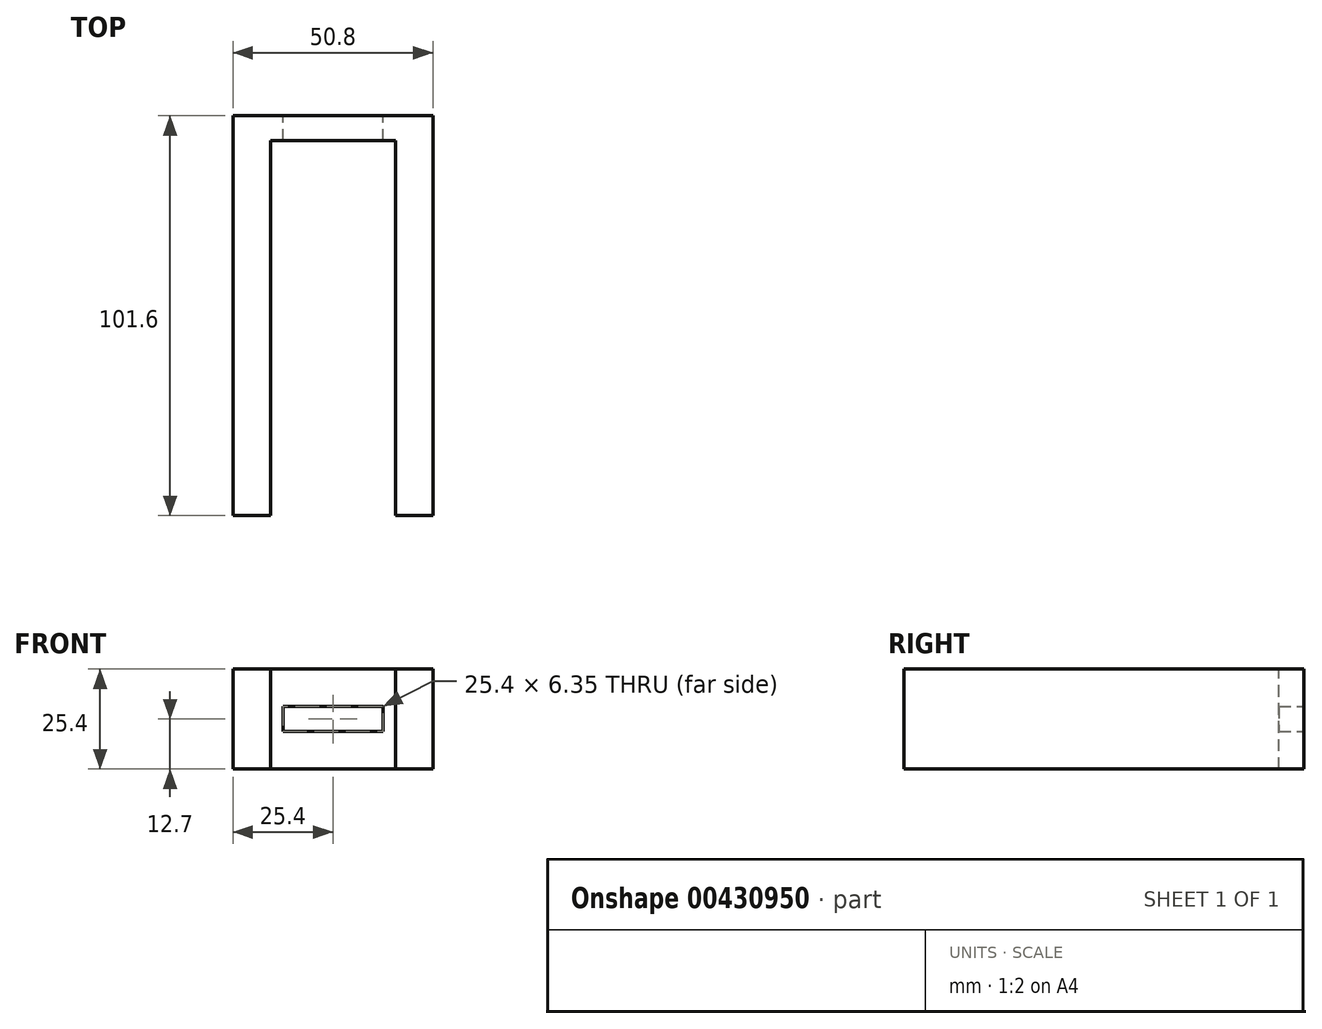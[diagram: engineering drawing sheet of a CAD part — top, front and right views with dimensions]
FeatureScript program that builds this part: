
annotation { "Feature Type Name" : "Feature", "Feature Type Description" : "" }
export const myFeature = defineFeature(function(context is Context, id is Id, definition is map)
    precondition{}
    {
        {
            var Q0;
            Q0=qCreatedBy(makeId("Front.planeOp"),FACE);
            var sketch = newSketch(context, id + "F0", { "sketchPlane" : qUnion([Q0])});
            skLineSegment(sketch, "E0.bottom", {"start": v(25.4, -12.7) * mm, "end": v(-25.4, -12.7) * mm});
            skLineSegment(sketch, "E0.top", {"start": v(25.4, 12.7) * mm, "end": v(-25.4, 12.7) * mm});
            skLineSegment(sketch, "E0.left", {"start": v(25.4, -12.7) * mm, "end": v(25.4, 12.7) * mm});
            skLineSegment(sketch, "E0.right", {"start": v(-25.4, -12.7) * mm, "end": v(-25.4, 12.7) * mm});
            skPoint(sketch, "E0.middle", {"position": v(0, 0) * mm});
            skLineSegment(sketch, "E1.bottom", {"start": v(12.7, 3.18) * mm, "end": v(-12.7, 3.18) * mm});
            skLineSegment(sketch, "E1.top", {"start": v(12.7, -3.17) * mm, "end": v(-12.7, -3.17) * mm});
            skLineSegment(sketch, "E1.left", {"start": v(12.7, 3.18) * mm, "end": v(12.7, -3.18) * mm});
            skLineSegment(sketch, "E1.right", {"start": v(-12.7, 3.18) * mm, "end": v(-12.7, -3.18) * mm});
            skLineSegment(sketch, "E2", {"start": v(-12.7, -3.17) * mm, "end": v(-12.7, -12.7) * mm});
            skLineSegment(sketch, "E3", {"start": v(-12.7, 3.18) * mm, "end": v(-12.7, 12.7) * mm});
            skLineSegment(sketch, "E4", {"start": v(12.7, -3.17) * mm, "end": v(12.7, -12.7) * mm});
            skLineSegment(sketch, "E5", {"start": v(12.7, 3.18) * mm, "end": v(12.7, 12.7) * mm});
            skLineSegment(sketch, "E6", {"start": v(15.88, 12.7) * mm, "end": v(15.88, -12.7) * mm});
            skLineSegment(sketch, "E7", {"start": v(-15.88, 12.7) * mm, "end": v(-15.88, -12.7) * mm});
            skSolve(sketch);
        }
        {
            var Q0;
            Q0 = qSketchRegion(id + "F0", true);
            extrude(context, id + "F1", {"entities" : qUnion([Q0]), "depth" : 6.35 * mm});
        }
        {
            var Q0;
            {var subQ0=sQuery(id+"F0.wireOp",EDGE,"E0.left");Q0=makeQuery(id+"F0.imprint","IMPRINT",FACE,{"disambiguationData":[TD([[makeQuery(id+"F0.imprint","IMPRINT",EDGE,{"derivedFrom":subQ0}),1.0]])]});}
            var Q1;
            {var subQ0=sQuery(id+"F0.wireOp",EDGE,"E0.right");Q1=makeQuery(id+"F0.imprint","IMPRINT",FACE,{"disambiguationData":[TD([[makeQuery(id+"F0.imprint","IMPRINT",EDGE,{"derivedFrom":subQ0}),-1.0]])]});}
            extrude(context, id + "F2", {"entities" : qUnion([Q0, Q1]), "operationType" : NewBodyOperationType.ADD, "depth" : 101.6 * mm});
        }
    });
